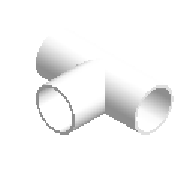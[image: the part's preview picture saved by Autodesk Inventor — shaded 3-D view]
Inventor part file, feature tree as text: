
AUTODESK INVENTOR PART (.ipt)
format: ipt  version: 2023 (Build 270158000, 158)  size: 204,800 bytes
history: native  units: mm (DEFAULTED — no unit token found)
features: other x9, revolve x4, sketch x3
ambient origin geometry x8: Origin, YZ Plane, XZ Plane, XY Plane, X Axis, Y Axis, Z Axis, Center Point
bodies: Solid1 (feature_tree)
feature tree (16):
  revolve  "Revolution1"  [1 undecoded]
  revolve  "Revolution2"  Angle=90.0deg
  revolve  "Revolution3"  [1 undecoded]
  revolve  "Revolution4"  Angle=90.0deg
  other  "Work Axis1"
  other  "Work Point1"
  other  "Work Point2"
  other  "Work Axis2"
  other  "Work Point3"
  other  "Work Point4"
  other  "Work Axis3"
  other  "Work Point5"
  other  "Work Point6"
  sketch  "Sketch1"  dims[d1=110.0mm d0=234.0mm]
  sketch  "Sketch3"  dims[d2=126.4mm d7=90.0deg]
  sketch  "Sketch4"  dims[d3=126.4mm d4=117.0mm d13=90.0deg d5=110.0mm d6=88.0mm d8=61.0mm d17=90.0deg d9=110.0mm d10=110.0mm d11=88.0mm d12=61.0mm d14=61.0mm d23=90.0deg]
note: 2 required parameter values undecoded (feature->parameter linkage not recoverable at this tier; creation-order binding heuristic only, values carry confidence <= 0.55)
